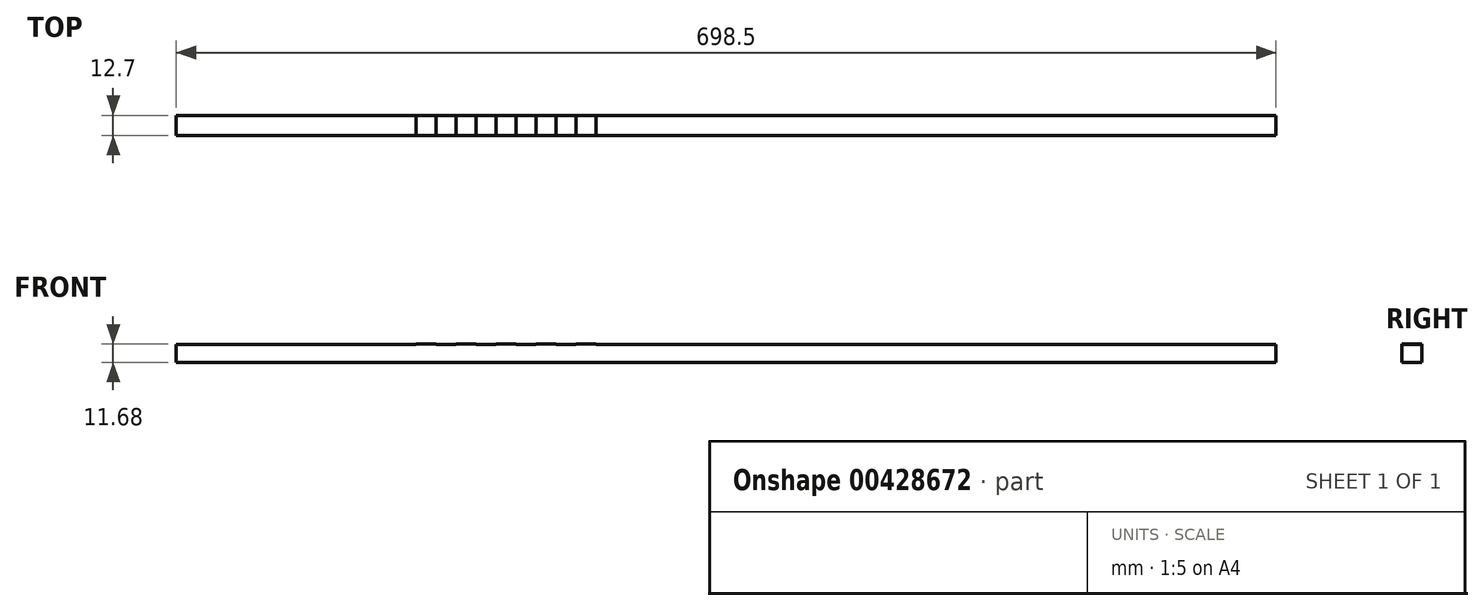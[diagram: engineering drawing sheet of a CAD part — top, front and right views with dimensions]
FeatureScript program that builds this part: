
annotation { "Feature Type Name" : "Feature", "Feature Type Description" : "" }
export const myFeature = defineFeature(function(context is Context, id is Id, definition is map)
    precondition{}
    {
        {
            var Q0;
            Q0=qCreatedBy(makeId("Top.planeOp"),FACE);
            var sketch = newSketch(context, id + "F0", { "sketchPlane" : qUnion([Q0])});
            skLineSegment(sketch, "E0.bottom", {"start": v(-349.25, 6.35) * mm, "end": v(349.25, 6.35) * mm});
            skLineSegment(sketch, "E0.top", {"start": v(-349.25, -6.35) * mm, "end": v(349.25, -6.35) * mm});
            skLineSegment(sketch, "E0.left", {"start": v(-349.25, 6.35) * mm, "end": v(-349.25, -6.35) * mm});
            skLineSegment(sketch, "E0.right", {"start": v(349.25, 6.35) * mm, "end": v(349.25, -6.35) * mm});
            skPoint(sketch, "E0.middle", {"position": v(0, 0) * mm});
            skLineSegment(sketch, "E1", {"start": v(-196.85, -6.35) * mm, "end": v(-196.85, 6.35) * mm});
            skLineSegment(sketch, "E2", {"start": v(-196.85, 6.35) * mm, "end": v(-184.15, 6.35) * mm});
            skLineSegment(sketch, "E3", {"start": v(-184.15, 6.35) * mm, "end": v(-184.15, -6.35) * mm});
            skLineSegment(sketch, "E4", {"start": v(-184.15, -6.35) * mm, "end": v(-171.45, -6.35) * mm});
            skLineSegment(sketch, "E5", {"start": v(-171.45, -6.35) * mm, "end": v(-171.45, 6.35) * mm});
            skLineSegment(sketch, "E6", {"start": v(-171.45, 6.35) * mm, "end": v(-158.75, 6.35) * mm});
            skLineSegment(sketch, "E7", {"start": v(-158.75, 6.35) * mm, "end": v(-158.75, -6.35) * mm});
            skLineSegment(sketch, "E8", {"start": v(-158.75, -6.35) * mm, "end": v(-146.05, -6.35) * mm});
            skLineSegment(sketch, "E9", {"start": v(-146.05, -6.35) * mm, "end": v(-146.05, 6.35) * mm});
            skLineSegment(sketch, "E10", {"start": v(-146.05, 6.35) * mm, "end": v(-133.35, 6.35) * mm});
            skLineSegment(sketch, "E11", {"start": v(-133.35, 6.35) * mm, "end": v(-133.35, -6.35) * mm});
            skLineSegment(sketch, "E12", {"start": v(-133.35, -6.35) * mm, "end": v(-120.65, -6.35) * mm});
            skLineSegment(sketch, "E13", {"start": v(-120.65, -6.35) * mm, "end": v(-120.65, 6.35) * mm});
            skLineSegment(sketch, "E14", {"start": v(-120.65, 6.35) * mm, "end": v(-107.95, 6.35) * mm});
            skLineSegment(sketch, "E15", {"start": v(-107.95, 6.35) * mm, "end": v(-107.95, -6.35) * mm});
            skLineSegment(sketch, "E16", {"start": v(-107.95, -6.35) * mm, "end": v(-95.25, -6.35) * mm});
            skLineSegment(sketch, "E17", {"start": v(-95.25, -6.35) * mm, "end": v(-95.25, 6.35) * mm});
            skLineSegment(sketch, "E18", {"start": v(-95.25, 6.35) * mm, "end": v(-82.55, 6.35) * mm});
            skLineSegment(sketch, "E19", {"start": v(-82.55, 6.35) * mm, "end": v(-82.55, -6.35) * mm});
            skLineSegment(sketch, "E20", {"start": v(-82.55, -6.35) * mm, "end": v(-69.85, -6.35) * mm});
            skLineSegment(sketch, "E21", {"start": v(-69.85, -6.35) * mm, "end": v(-69.85, 6.35) * mm});
            skLineSegment(sketch, "E22", {"start": v(-69.85, 6.35) * mm, "end": v(-57.15, 6.35) * mm});
            skLineSegment(sketch, "E23", {"start": v(-57.15, 6.35) * mm, "end": v(-57.15, -6.35) * mm});
            skLineSegment(sketch, "E24", {"start": v(-57.15, -6.35) * mm, "end": v(-44.45, -6.35) * mm});
            skLineSegment(sketch, "E25", {"start": v(-44.45, -6.35) * mm, "end": v(-44.45, 6.35) * mm});
            skLineSegment(sketch, "E26", {"start": v(-44.45, 6.35) * mm, "end": v(-31.75, 6.35) * mm});
            skLineSegment(sketch, "E27", {"start": v(-31.75, 6.35) * mm, "end": v(-31.75, -6.35) * mm});
            skLineSegment(sketch, "E28", {"start": v(-31.75, -6.35) * mm, "end": v(-19.05, -6.35) * mm});
            skLineSegment(sketch, "E29", {"start": v(-19.05, -6.35) * mm, "end": v(-19.05, 6.35) * mm});
            skSolve(sketch);
        }
        {
            var Q0;
            Q0 = qSketchRegion(id + "F0", true);
            extrude(context, id + "F1", {"entities" : qUnion([Q0]), "depth" : 11.43 * mm});
        }
        {
            var Q0;
            {var subQ0=sQuery(id+"F0.wireOp",EDGE,"E1");Q0=makeQuery(id+"F0.imprint","IMPRINT",FACE,{"disambiguationData":[TD([[makeQuery(id+"F0.imprint","IMPRINT",EDGE,{"derivedFrom":subQ0}),-1.0]])]});}
            var Q1;
            {var subQ0=sQuery(id+"F0.wireOp",EDGE,"E5");Q1=makeQuery(id+"F0.imprint","IMPRINT",FACE,{"disambiguationData":[TD([[makeQuery(id+"F0.imprint","IMPRINT",EDGE,{"derivedFrom":subQ0}),-1.0]])]});}
            var Q2;
            {var subQ0=sQuery(id+"F0.wireOp",EDGE,"E9");Q2=makeQuery(id+"F0.imprint","IMPRINT",FACE,{"disambiguationData":[TD([[makeQuery(id+"F0.imprint","IMPRINT",EDGE,{"derivedFrom":subQ0}),-1.0]])]});}
            var Q3;
            {var subQ0=sQuery(id+"F0.wireOp",EDGE,"E13");Q3=makeQuery(id+"F0.imprint","IMPRINT",FACE,{"disambiguationData":[TD([[makeQuery(id+"F0.imprint","IMPRINT",EDGE,{"derivedFrom":subQ0}),-1.0]])]});}
            var Q4;
            {var subQ0=sQuery(id+"F0.wireOp",EDGE,"E17");Q4=makeQuery(id+"F0.imprint","IMPRINT",FACE,{"disambiguationData":[TD([[makeQuery(id+"F0.imprint","IMPRINT",EDGE,{"derivedFrom":subQ0}),-1.0]])]});}
            extrude(context, id + "F2", {"entities" : qUnion([Q0, Q1, Q2, Q3, Q4]), "operationType" : NewBodyOperationType.ADD, "depth" : 11.68 * mm});
        }
    });
